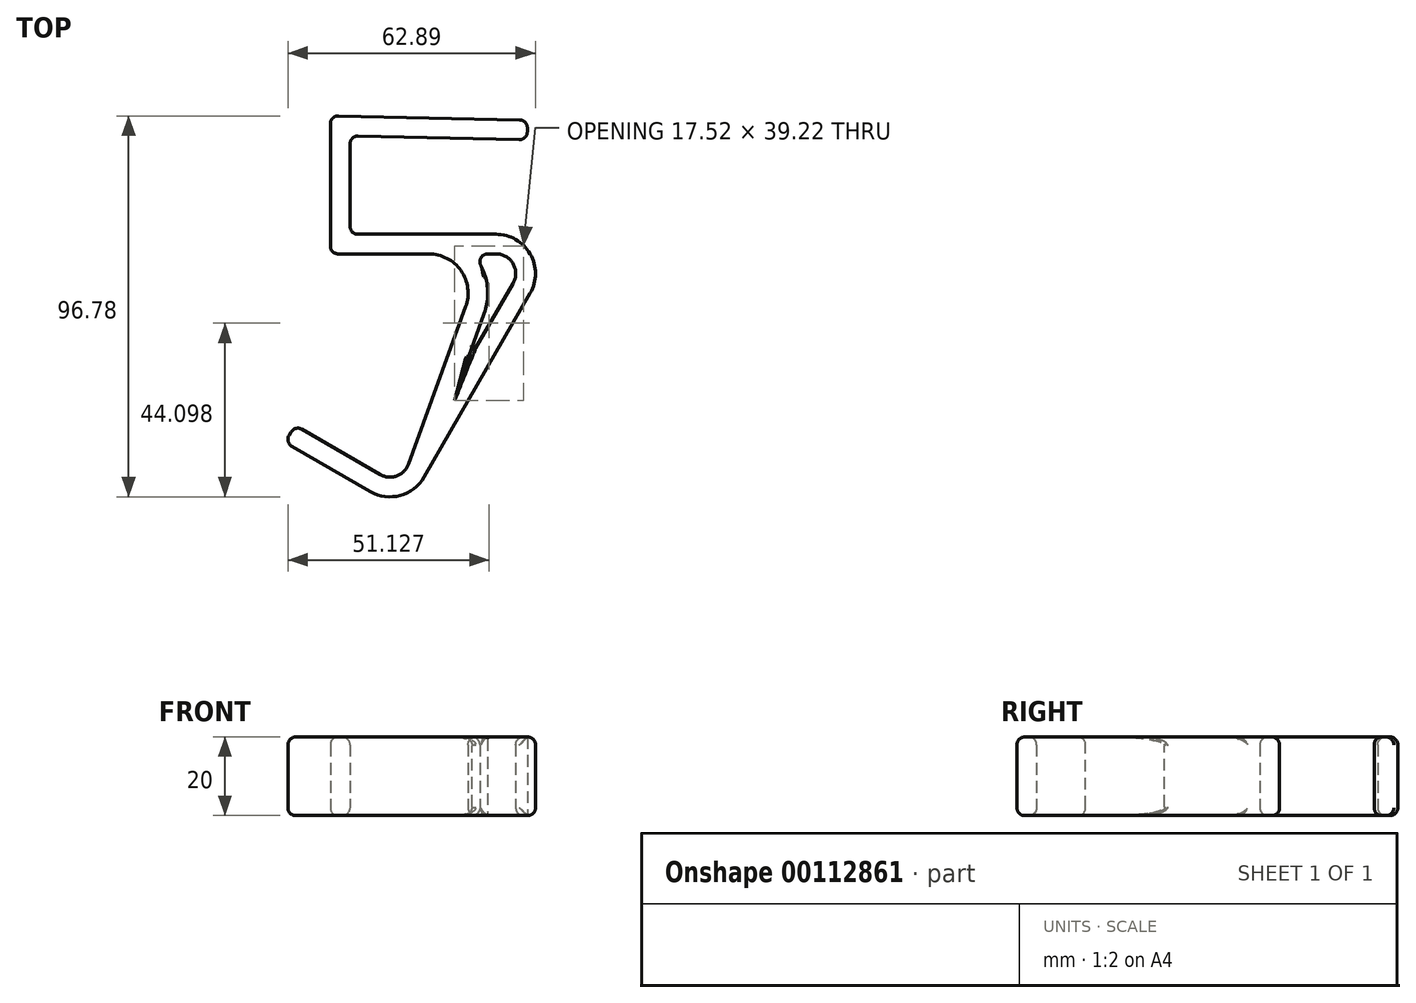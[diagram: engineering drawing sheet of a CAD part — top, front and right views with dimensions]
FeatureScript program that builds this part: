
annotation { "Feature Type Name" : "Feature", "Feature Type Description" : "" }
export const myFeature = defineFeature(function(context is Context, id is Id, definition is map)
    precondition{}
    {
        {
            var Q0;
            Q0=qCreatedBy(makeId("Top.planeOp"),FACE);
            var sketch = newSketch(context, id + "F0", { "sketchPlane" : qUnion([Q0])});
            skLineSegment(sketch, "E0.top", {"start": v(14.6, -12.5) * mm, "end": v(-22.5, -12.5) * mm});
            skLineSegment(sketch, "E0.right", {"start": v(-22.5, 12.5) * mm, "end": v(-22.5, -12.5) * mm});
            skPoint(sketch, "E0.middle", {"position": v(0, 0) * mm});
            skLineSegment(sketch, "E1", {"start": v(-22.5, 12.5) * mm, "end": v(22.5, 11.5) * mm});
            skLineSegment(sketch, "E2", {"start": v(6.9, -30.92) * mm, "end": v(-7.66, -70.92) * mm});
            skLineSegment(sketch, "E3", {"start": v(-14.86, -73.54) * mm, "end": v(-36.51, -61.04) * mm});
            skLineSegment(sketch, "E4.0", {"start": v(-27.5, 17.61) * mm, "end": v(22.61, 16.5) * mm});
            skLineSegment(sketch, "E4.1", {"start": v(-27.5, 17.61) * mm, "end": v(-27.5, -17.5) * mm});
            skLineSegment(sketch, "E4.2", {"start": v(-2.5, -17.5) * mm, "end": v(-27.5, -17.5) * mm});
            skPoint(sketch, "E5.visualSharp", {"position": v(-9.7, -76.52) * mm});
            skArc(sketch, "E5.filletArc", {"start": v(-14.86, -73.54) * mm, "mid": v(-10.65, -73.9) * mm, "end": v(-7.66, -70.92) * mm});
            skArc(sketch, "E6.filletArc", {"start": v(6.9, -30.92) * mm, "mid": v(5.7, -21.76) * mm, "end": v(-2.5, -17.5) * mm});
            skLineSegment(sketch, "E7.0", {"start": v(-17.36, -77.87) * mm, "end": v(-39.01, -65.37) * mm});
            skArc(sketch, "E7.1", {"start": v(-17.36, -77.87) * mm, "mid": v(-9.77, -78.87) * mm, "end": v(-3.7, -74.21) * mm});
            skLineSegment(sketch, "E7.2", {"start": v(11.6, -32.63) * mm, "end": v(6.59, -46.4) * mm});
            skArc(sketch, "E7.3", {"start": v(11.6, -32.63) * mm, "mid": v(12.23, -24.66) * mm, "end": v(8.68, -17.5) * mm});
            skLineSegment(sketch, "E8", {"start": v(-3.7, -74.21) * mm, "end": v(23.27, -27.5) * mm});
            skArc(sketch, "E9.filletArc", {"start": v(23.27, -27.5) * mm, "mid": v(23.27, -17.5) * mm, "end": v(14.6, -12.5) * mm});
            skLineSegment(sketch, "E10.0", {"start": v(14.6, -17.5) * mm, "end": v(-22.5, -17.5) * mm});
            skArc(sketch, "E10.1", {"start": v(18.94, -25) * mm, "mid": v(18.94, -20) * mm, "end": v(14.6, -17.5) * mm});
            skLineSegment(sketch, "E10.2", {"start": v(6.59, -46.4) * mm, "end": v(18.94, -25) * mm});
            skArc(sketch, "E11", {"start": v(8.68, -17.5) * mm, "mid": v(3.62, -13.8) * mm, "end": v(-2.5, -12.5) * mm, "construction": true});
            skLineSegment(sketch, "E12", {"start": v(22.61, 16.5) * mm, "end": v(22.5, 11.5) * mm});
            skLineSegment(sketch, "E13", {"start": v(-39.01, -65.37) * mm, "end": v(-36.51, -61.04) * mm});
            skSolve(sketch);
        }
        {
            var Q0;
            Q0 = qSketchRegion(id + "F0", true);
            var Q1;
            Q1=makeQuery(id+"F0.imprint","IMPRINT",FACE,{"disambiguationData":[TD([[makeQuery(id+"F0.imprint","IMPRINT",EDGE,{"derivedFrom":sQuery(id+"F0.wireOp",EDGE,"E0.top")}),1.0]])]});
            extrude(context, id + "F1", {"entities" : qUnion([Q0, Q1]), "depth" : 20 * mm});
        }
        {
            var Q0;
            Q0=makeQuery(id+"F1.opExtrude","SWEPT_FACE",FACE,{"disambiguationData":[OSD([sQuery(id+"F0.wireOp",EDGE,"E4.1")])]});
            var Q1;
            Q1=makeQuery(id+"F1.opExtrude","SWEPT_FACE",FACE,{"disambiguationData":[OSD([sQuery(id+"F0.wireOp",EDGE,"E4.2"),sQuery(id+"F0.wireOp",EDGE,"E10.0")])]});
            var Q2;
            Q2=makeQuery(id+"F1.opExtrude","SWEPT_FACE",FACE,{"disambiguationData":[OSD([sQuery(id+"F0.wireOp",EDGE,"E4.0")])]});
            fillet(context, id + "F2", {"entities" : qUnion([Q0, Q1, Q2]), "radius" : 2 * mm, "tangentPropagation" : true, "allowEdgeOverflow" : false});
        }
        {
            var Q0;
            Q0=makeQuery(id+"F1.opExtrude","SWEPT_FACE",FACE,{"disambiguationData":[OSD([sQuery(id+"F0.wireOp",EDGE,"E8")])]});
            fillet(context, id + "F3", {"entities" : qUnion([Q0]), "radius" : 2 * mm, "tangentPropagation" : true, "allowEdgeOverflow" : false});
        }
        {
            var Q0;
            Q0=makeQuery(id+"F1.opExtrude","SWEPT_FACE",FACE,{"disambiguationData":[OSD([sQuery(id+"F0.wireOp",EDGE,"E1")])]});
            var Q1;
            Q1=makeQuery(id+"F1.opExtrude","SWEPT_FACE",FACE,{"disambiguationData":[OSD([sQuery(id+"F0.wireOp",EDGE,"E0.right")])]});
            fillet(context, id + "F4", {"entities" : qUnion([Q0, Q1]), "radius" : 2 * mm, "allowEdgeOverflow" : false});
        }
        {
            var Q0;
            Q0=makeQuery(id+"F1.opExtrude","SWEPT_FACE",FACE,{"disambiguationData":[OSD([sQuery(id+"F0.wireOp",EDGE,"E13")])]});
            fillet(context, id + "F5", {"entities" : qUnion([Q0]), "radius" : 2 * mm, "tangentPropagation" : true, "allowEdgeOverflow" : false});
        }
        {
            var Q0;
            Q0=makeQuery(id+"F1.opExtrude","SWEPT_FACE",FACE,{"disambiguationData":[OSD([sQuery(id+"F0.wireOp",EDGE,"E7.3")])]});
            var Q1;
            Q1=makeQuery(id+"F1.opExtrude","SWEPT_FACE",FACE,{"disambiguationData":[OSD([sQuery(id+"F0.wireOp",EDGE,"E7.2")])]});
            var Q2;
            Q2=makeQuery(id+"F1.opExtrude","SWEPT_FACE",FACE,{"disambiguationData":[OSD([sQuery(id+"F0.wireOp",EDGE,"E10.0")])]});
            var Q3;
            Q3=makeQuery(id+"F1.opExtrude","SWEPT_FACE",FACE,{"disambiguationData":[OSD([sQuery(id+"F0.wireOp",EDGE,"E10.1")])]});
            var Q4;
            Q4=makeQuery(id+"F1.opExtrude","SWEPT_FACE",FACE,{"disambiguationData":[OSD([sQuery(id+"F0.wireOp",EDGE,"E10.2")])]});
            fillet(context, id + "F6", {"entities" : qUnion([Q0, Q1, Q2, Q3, Q4]), "radius" : 0.5 * mm, "tangentPropagation" : true, "allowEdgeOverflow" : false});
        }
    });
